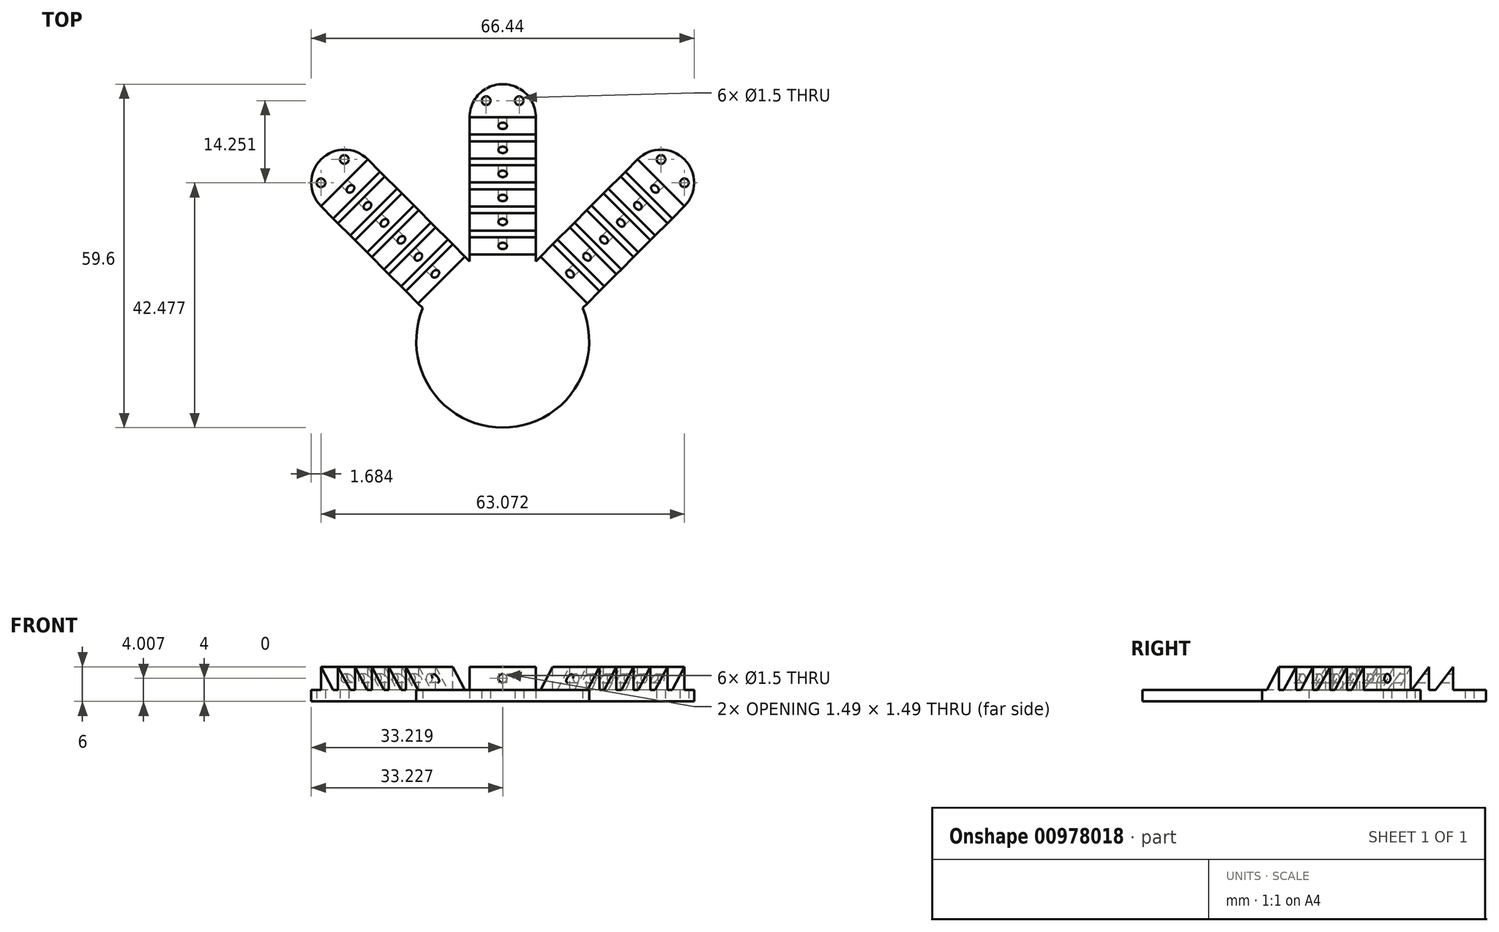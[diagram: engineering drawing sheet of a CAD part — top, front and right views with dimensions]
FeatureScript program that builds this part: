
annotation { "Feature Type Name" : "Feature", "Feature Type Description" : "" }
export const myFeature = defineFeature(function(context is Context, id is Id, definition is map)
    precondition{}
    {
        {
            var Q0;
            Q0=qCreatedBy(makeId("Top.planeOp"),FACE);
            var sketch = newSketch(context, id + "F0", { "sketchPlane" : qUnion([Q0])});
            skArc(sketch, "E0", {"start": v(-13.86, 5.74) * mm, "mid": v(0, -15) * mm, "end": v(13.86, 5.74) * mm});
            skLineSegment(sketch, "E1", {"start": v(-5.74, 13.86) * mm, "end": v(-5.74, 38.86) * mm});
            skLineSegment(sketch, "E2", {"start": v(5.74, 38.86) * mm, "end": v(5.74, 13.86) * mm});
            skArc(sketch, "E3", {"start": v(5.74, 38.86) * mm, "mid": v(0, 44.6) * mm, "end": v(-5.74, 38.86) * mm});
            skLineSegment(sketch, "E4", {"start": v(-5.74, 13.86) * mm, "end": v(-23.42, 31.54) * mm});
            skLineSegment(sketch, "E5", {"start": v(-13.86, 5.74) * mm, "end": v(-31.54, 23.42) * mm});
            skArc(sketch, "E6", {"start": v(-23.42, 31.54) * mm, "mid": v(-31.54, 31.54) * mm, "end": v(-31.54, 23.42) * mm});
            skLineSegment(sketch, "E7", {"start": v(5.74, 13.86) * mm, "end": v(23.42, 31.54) * mm});
            skLineSegment(sketch, "E8", {"start": v(13.86, 5.74) * mm, "end": v(31.54, 23.42) * mm});
            skArc(sketch, "E9", {"start": v(31.54, 23.42) * mm, "mid": v(31.54, 31.54) * mm, "end": v(23.42, 31.54) * mm});
            skLineSegment(sketch, "E10", {"start": v(-5.74, 13.86) * mm, "end": v(-13.86, 5.74) * mm, "construction": true});
            skLineSegment(sketch, "E11", {"start": v(5.74, 13.86) * mm, "end": v(13.86, 5.74) * mm, "construction": true});
            skLineSegment(sketch, "E12", {"start": v(-23.42, 31.54) * mm, "end": v(-31.54, 23.42) * mm, "construction": true});
            skLineSegment(sketch, "E13", {"start": v(-31.54, 23.42) * mm, "end": v(-31.54, 31.54) * mm, "construction": true});
            skLineSegment(sketch, "E14", {"start": v(-31.54, 31.54) * mm, "end": v(-23.42, 31.54) * mm, "construction": true});
            skCircle(sketch, "E15", {"center": v(-31.54, 27.48) * mm, "radius": 0.75 * mm});
            skCircle(sketch, "E16", {"center": v(-27.48, 31.54) * mm, "radius": 0.75 * mm});
            skLineSegment(sketch, "E17", {"start": v(-5.74, 38.86) * mm, "end": v(0, 44.6) * mm, "construction": true});
            skLineSegment(sketch, "E18", {"start": v(0, 44.6) * mm, "end": v(5.74, 38.86) * mm, "construction": true});
            skLineSegment(sketch, "E19", {"start": v(23.42, 31.54) * mm, "end": v(31.54, 31.54) * mm, "construction": true});
            skLineSegment(sketch, "E20", {"start": v(31.54, 31.54) * mm, "end": v(31.54, 23.42) * mm, "construction": true});
            skCircle(sketch, "E21", {"center": v(-2.87, 41.73) * mm, "radius": 0.75 * mm});
            skCircle(sketch, "E22", {"center": v(2.87, 41.73) * mm, "radius": 0.75 * mm});
            skCircle(sketch, "E23", {"center": v(27.48, 31.54) * mm, "radius": 0.75 * mm});
            skCircle(sketch, "E24", {"center": v(31.54, 27.48) * mm, "radius": 0.75 * mm});
            skSolve(sketch);
        }
        {
            var Q0;
            Q0 = qSketchRegion(id + "F0", true);
            extrude(context, id + "F1", {"entities" : qUnion([Q0]), "depth" : 2 * mm, "offsetDistance" : 25 * mm});
        }
        {
            var Q0;
            Q0=makeQuery(id+"F1.opExtrude","CAP_EDGE",EDGE,{"disambiguationData":[OSD([sQuery(id+"F0.wireOp",EDGE,"E7")])],"isStart":false});
            cPlane(context, id + "F2", {"entities" : qUnion([Q0]), "cplaneType" : CPlaneType.LINE_ANGLE, "offset" : 25 * mm, "angle" : 90 * degree, "width" : 150 * mm, "height" : 150 * mm});
        }
        {
            var Q0;
            Q0=qCreatedBy(id+"F2.planeOp",FACE);
            var sketch = newSketch(context, id + "F3", { "sketchPlane" : qUnion([Q0])});
            skLineSegment(sketch, "E25", {"start": v(38.86, 2) * mm, "end": v(38.86, 6) * mm});
            skLineSegment(sketch, "E26", {"start": v(38.86, 2) * mm, "end": v(35.86, 2) * mm});
            skLineSegment(sketch, "E27", {"start": v(35.86, 2) * mm, "end": v(38.86, 6) * mm});
            skLineSegment(sketch, "E28.1.0.0", {"start": v(34.7, 2) * mm, "end": v(34.7, 6) * mm});
            skLineSegment(sketch, "E28.1.0.1", {"start": v(31.7, 2) * mm, "end": v(34.7, 6) * mm});
            skLineSegment(sketch, "E28.1.0.2", {"start": v(34.7, 2) * mm, "end": v(31.7, 2) * mm});
            skLineSegment(sketch, "E28.2.0.0", {"start": v(30.52, 2) * mm, "end": v(30.52, 6) * mm});
            skLineSegment(sketch, "E28.2.0.1", {"start": v(27.52, 2) * mm, "end": v(30.52, 6) * mm});
            skLineSegment(sketch, "E28.2.0.2", {"start": v(30.52, 2) * mm, "end": v(27.52, 2) * mm});
            skLineSegment(sketch, "E28.3.0.0", {"start": v(26.36, 2) * mm, "end": v(26.36, 6) * mm});
            skLineSegment(sketch, "E28.3.0.1", {"start": v(23.36, 2) * mm, "end": v(26.36, 6) * mm});
            skLineSegment(sketch, "E28.3.0.2", {"start": v(26.36, 2) * mm, "end": v(23.36, 2) * mm});
            skLineSegment(sketch, "E28.4.0.0", {"start": v(22.2, 2) * mm, "end": v(22.2, 6) * mm});
            skLineSegment(sketch, "E28.4.0.1", {"start": v(19.2, 2) * mm, "end": v(22.2, 6) * mm});
            skLineSegment(sketch, "E28.4.0.2", {"start": v(22.2, 2) * mm, "end": v(19.2, 2) * mm});
            skLineSegment(sketch, "E28.5.0.0", {"start": v(18.02, 2) * mm, "end": v(18.02, 6) * mm});
            skLineSegment(sketch, "E28.5.0.1", {"start": v(15.02, 2) * mm, "end": v(18.02, 6) * mm});
            skLineSegment(sketch, "E28.5.0.2", {"start": v(18.02, 2) * mm, "end": v(15.02, 2) * mm});
            skLineSegment(sketch, "E28.direction1", {"start": v(38.86, 2) * mm, "end": v(34.7, 2) * mm, "construction": true});
            skSolve(sketch);
        }
        {
            var Q0;
            Q0 = qSketchRegion(id + "F3", true);
            extrude(context, id + "F4", {"entities" : qUnion([Q0]), "operationType" : NewBodyOperationType.ADD, "depth" : (11.48) * mm, "offsetDistance" : 25 * mm});
        }
        {
            var Q0;
            Q0=makeQuery(id+"F1.opExtrude","SWEPT_FACE",FACE,{"disambiguationData":[OSD([sQuery(id+"F0.wireOp",EDGE,"E1")])]});
            var sketch = newSketch(context, id + "F5", { "sketchPlane" : qUnion([Q0])});
            skLineSegment(sketch, "E29", {"start": v(-38.86, 2) * mm, "end": v(-38.86, 6) * mm});
            skLineSegment(sketch, "E30", {"start": v(-38.86, 2) * mm, "end": v(-35.86, 2) * mm});
            skLineSegment(sketch, "E31", {"start": v(-35.86, 2) * mm, "end": v(-38.86, 6) * mm});
            skLineSegment(sketch, "E32.1.0.0", {"start": v(-34.7, 2) * mm, "end": v(-34.7, 6) * mm});
            skLineSegment(sketch, "E32.1.0.1", {"start": v(-31.7, 2) * mm, "end": v(-34.7, 6) * mm});
            skLineSegment(sketch, "E32.1.0.2", {"start": v(-34.7, 2) * mm, "end": v(-31.7, 2) * mm});
            skLineSegment(sketch, "E32.2.0.0", {"start": v(-30.52, 2) * mm, "end": v(-30.52, 6) * mm});
            skLineSegment(sketch, "E32.2.0.1", {"start": v(-27.52, 2) * mm, "end": v(-30.52, 6) * mm});
            skLineSegment(sketch, "E32.2.0.2", {"start": v(-30.52, 2) * mm, "end": v(-27.52, 2) * mm});
            skLineSegment(sketch, "E32.3.0.0", {"start": v(-26.36, 2) * mm, "end": v(-26.36, 6) * mm});
            skLineSegment(sketch, "E32.3.0.1", {"start": v(-23.36, 2) * mm, "end": v(-26.36, 6) * mm});
            skLineSegment(sketch, "E32.3.0.2", {"start": v(-26.36, 2) * mm, "end": v(-23.36, 2) * mm});
            skLineSegment(sketch, "E32.4.0.0", {"start": v(-22.2, 2) * mm, "end": v(-22.2, 6) * mm});
            skLineSegment(sketch, "E32.4.0.1", {"start": v(-19.2, 2) * mm, "end": v(-22.2, 6) * mm});
            skLineSegment(sketch, "E32.4.0.2", {"start": v(-22.2, 2) * mm, "end": v(-19.2, 2) * mm});
            skLineSegment(sketch, "E32.5.0.0", {"start": v(-18.02, 2) * mm, "end": v(-18.02, 6) * mm});
            skLineSegment(sketch, "E32.5.0.1", {"start": v(-15.02, 2) * mm, "end": v(-18.02, 6) * mm});
            skLineSegment(sketch, "E32.5.0.2", {"start": v(-18.02, 2) * mm, "end": v(-15.02, 2) * mm});
            skLineSegment(sketch, "E32.direction1", {"start": v(-38.86, 2) * mm, "end": v(-34.7, 2) * mm, "construction": true});
            skSolve(sketch);
        }
        {
            var Q0;
            Q0 = qSketchRegion(id + "F5", true);
            extrude(context, id + "F6", {"entities" : qUnion([Q0]), "operationType" : NewBodyOperationType.ADD, "oppositeDirection" : true, "depth" : (11.48) * mm, "offsetDistance" : 25 * mm});
        }
        {
            var Q0;
            Q0=makeQuery(id+"F1.opExtrude","SWEPT_FACE",FACE,{"disambiguationData":[OSD([sQuery(id+"F0.wireOp",EDGE,"E5")])]});
            var sketch = newSketch(context, id + "F7", { "sketchPlane" : qUnion([Q0])});
            skLineSegment(sketch, "E33", {"start": v(-38.86, 2) * mm, "end": v(-38.86, 6) * mm});
            skLineSegment(sketch, "E34", {"start": v(-38.86, 6) * mm, "end": v(-35.86, 2) * mm});
            skLineSegment(sketch, "E35", {"start": v(-35.86, 2) * mm, "end": v(-38.86, 2) * mm});
            skLineSegment(sketch, "E36.1.0.0", {"start": v(-34.7, 6) * mm, "end": v(-31.7, 2) * mm});
            skLineSegment(sketch, "E36.1.0.1", {"start": v(-34.7, 2) * mm, "end": v(-34.7, 6) * mm});
            skLineSegment(sketch, "E36.1.0.2", {"start": v(-31.7, 2) * mm, "end": v(-34.7, 2) * mm});
            skLineSegment(sketch, "E36.2.0.0", {"start": v(-30.52, 6) * mm, "end": v(-27.52, 2) * mm});
            skLineSegment(sketch, "E36.2.0.1", {"start": v(-30.52, 2) * mm, "end": v(-30.52, 6) * mm});
            skLineSegment(sketch, "E36.2.0.2", {"start": v(-27.52, 2) * mm, "end": v(-30.52, 2) * mm});
            skLineSegment(sketch, "E36.3.0.0", {"start": v(-26.36, 6) * mm, "end": v(-23.36, 2) * mm});
            skLineSegment(sketch, "E36.3.0.1", {"start": v(-26.36, 2) * mm, "end": v(-26.36, 6) * mm});
            skLineSegment(sketch, "E36.3.0.2", {"start": v(-23.36, 2) * mm, "end": v(-26.36, 2) * mm});
            skLineSegment(sketch, "E36.4.0.0", {"start": v(-22.2, 6) * mm, "end": v(-19.2, 2) * mm});
            skLineSegment(sketch, "E36.4.0.1", {"start": v(-22.2, 2) * mm, "end": v(-22.2, 6) * mm});
            skLineSegment(sketch, "E36.4.0.2", {"start": v(-19.2, 2) * mm, "end": v(-22.2, 2) * mm});
            skLineSegment(sketch, "E36.5.0.0", {"start": v(-18.02, 6) * mm, "end": v(-15.02, 2) * mm});
            skLineSegment(sketch, "E36.5.0.1", {"start": v(-18.02, 2) * mm, "end": v(-18.02, 6) * mm});
            skLineSegment(sketch, "E36.5.0.2", {"start": v(-15.02, 2) * mm, "end": v(-18.02, 2) * mm});
            skLineSegment(sketch, "E36.direction1", {"start": v(-38.86, 2) * mm, "end": v(-34.7, 2) * mm, "construction": true});
            skSolve(sketch);
        }
        {
            var Q0;
            Q0 = qSketchRegion(id + "F7", true);
            extrude(context, id + "F8", {"entities" : qUnion([Q0]), "operationType" : NewBodyOperationType.ADD, "oppositeDirection" : true, "depth" : 11.48 * mm, "offsetDistance" : 25 * mm});
        }
        {
            var Q0;
            Q0=makeQuery(id+"F8.opExtrude","SWEPT_FACE",FACE,{"disambiguationData":[OSD([sQuery(id+"F7.wireOp",EDGE,"E33")])]});
            var sketch = newSketch(context, id + "F9", { "sketchPlane" : qUnion([Q0])});
            skLineSegment(sketch, "E37", {"start": v(-5.74, 6) * mm, "end": v(5.74, 2) * mm, "construction": true});
            skLineSegment(sketch, "E38", {"start": v(5.74, 6) * mm, "end": v(-5.74, 2) * mm, "construction": true});
            skCircle(sketch, "E39", {"center": v(0, 4) * mm, "radius": 0.75 * mm});
            skSolve(sketch);
        }
        {
            var Q0;
            Q0 = qSketchRegion(id + "F9", true);
            extrude(context, id + "F10", {"entities" : qUnion([Q0]), "operationType" : NewBodyOperationType.REMOVE, "oppositeDirection" : true, "depth" : 25 * mm, "offsetDistance" : 25 * mm});
        }
        {
            var Q0;
            Q0=makeQuery(id+"F6.opExtrude","SWEPT_FACE",FACE,{"disambiguationData":[OSD([sQuery(id+"F5.wireOp",EDGE,"E29")])]});
            var sketch = newSketch(context, id + "F11", { "sketchPlane" : qUnion([Q0])});
            skLineSegment(sketch, "E40", {"start": v(5.74, 2) * mm, "end": v(-5.74, 6) * mm, "construction": true});
            skLineSegment(sketch, "E41", {"start": v(5.74, 6) * mm, "end": v(-5.74, 2) * mm, "construction": true});
            skCircle(sketch, "E42", {"center": v(0, 4) * mm, "radius": 0.75 * mm});
            skSolve(sketch);
        }
        {
            var Q0;
            Q0 = qSketchRegion(id + "F11", true);
            extrude(context, id + "F12", {"entities" : qUnion([Q0]), "operationType" : NewBodyOperationType.REMOVE, "oppositeDirection" : true, "depth" : 25 * mm, "offsetDistance" : 25 * mm});
        }
        {
            var Q0;
            Q0=makeQuery(id+"F4.opExtrude","SWEPT_FACE",FACE,{"disambiguationData":[OSD([sQuery(id+"F3.wireOp",EDGE,"E25")])]});
            var sketch = newSketch(context, id + "F13", { "sketchPlane" : qUnion([Q0])});
            skLineSegment(sketch, "E43", {"start": v(-5.74, 6) * mm, "end": v(5.74, 2) * mm, "construction": true});
            skLineSegment(sketch, "E44", {"start": v(5.74, 6) * mm, "end": v(-5.74, 2) * mm, "construction": true});
            skCircle(sketch, "E45", {"center": v(0, 4) * mm, "radius": 0.75 * mm});
            skSolve(sketch);
        }
        {
            var Q0;
            Q0 = qSketchRegion(id + "F13", true);
            extrude(context, id + "F14", {"entities" : qUnion([Q0]), "operationType" : NewBodyOperationType.REMOVE, "oppositeDirection" : true, "depth" : 25 * mm, "offsetDistance" : 25 * mm});
        }
    });
